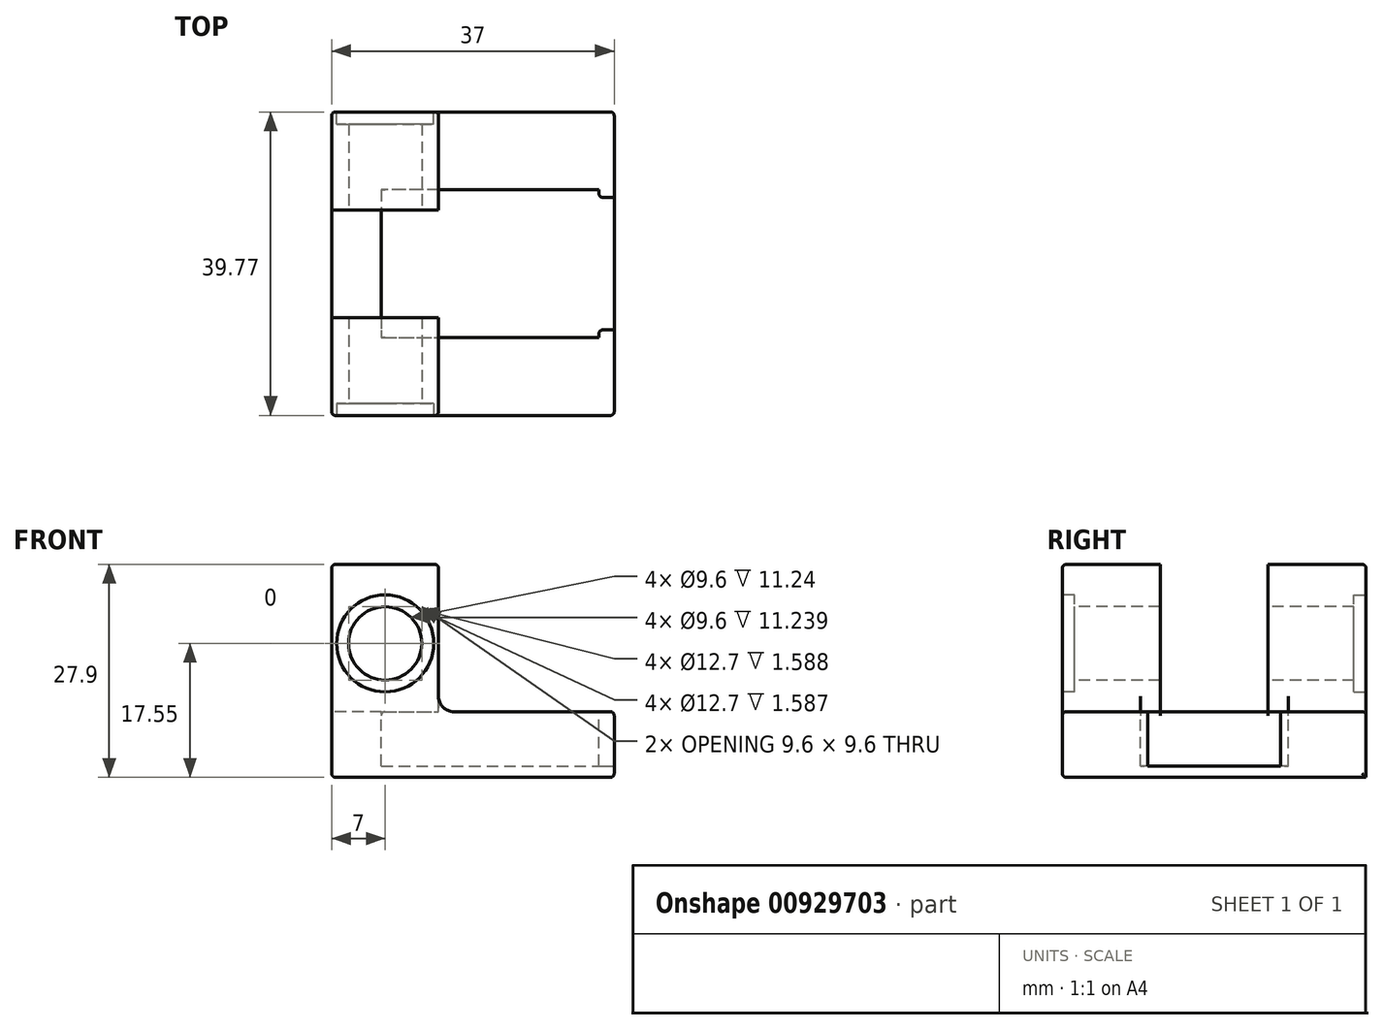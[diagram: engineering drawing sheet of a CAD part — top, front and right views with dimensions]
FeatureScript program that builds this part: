
annotation { "Feature Type Name" : "Feature", "Feature Type Description" : "" }
export const myFeature = defineFeature(function(context is Context, id is Id, definition is map)
    precondition{}
    {
        {
            var Q0;
            Q0=qCreatedBy(makeId("Front.planeOp"),FACE);
            var sketch = newSketch(context, id + "F0", { "sketchPlane" : qUnion([Q0])});
            skLineSegment(sketch, "E0", {"start": v(0, 0) * mm, "end": v(0, 27.9) * mm});
            skLineSegment(sketch, "E1", {"start": v(0, 27.9) * mm, "end": v(14, 27.9) * mm});
            skLineSegment(sketch, "E2", {"start": v(14, 27.9) * mm, "end": v(14, 8.6) * mm});
            skLineSegment(sketch, "E3", {"start": v(14, 8.6) * mm, "end": v(37, 8.6) * mm});
            skLineSegment(sketch, "E4", {"start": v(37, 8.6) * mm, "end": v(37, 0) * mm});
            skLineSegment(sketch, "E5", {"start": v(37, 0) * mm, "end": v(0, 0) * mm});
            skSolve(sketch);
        }
        {
            var Q0;
            Q0=makeQuery(id+"F0.imprint","IMPRINT",FACE,{"disambiguationData":[TD([[makeQuery(id+"F0.imprint","IMPRINT",EDGE,{"derivedFrom":sQuery(id+"F0.wireOp",EDGE,"E0")}),-1.0]])]});
            extrude(context, id + "F1", {"entities" : qUnion([Q0]), "depth" : 39.77 * mm, "offsetDistance" : 25 * mm});
        }
        {
            var Q0;
            Q0=makeQuery(id+"F1.opExtrude","CAP_FACE",FACE,{"disambiguationData":[OSD([sQuery(id+"F0.wireOp",EDGE,"E0"),sQuery(id+"F0.wireOp",EDGE,"E1"),sQuery(id+"F0.wireOp",EDGE,"E2"),sQuery(id+"F0.wireOp",EDGE,"E3"),sQuery(id+"F0.wireOp",EDGE,"E4"),sQuery(id+"F0.wireOp",EDGE,"E5")])],"isStart":false});
            var sketch = newSketch(context, id + "F2", { "sketchPlane" : qUnion([Q0])});
            skLineSegment(sketch, "E6", {"start": v(7, 27.9) * mm, "end": v(7, 23.9) * mm, "construction": true});
            skLineSegment(sketch, "E7", {"start": v(7, 23.9) * mm, "end": v(7, 0) * mm, "construction": true});
            skLineSegment(sketch, "E8", {"start": v(7, 23.9) * mm, "end": v(7, 17.55) * mm, "construction": true});
            skCircle(sketch, "E9", {"center": v(7, 17.55) * mm, "radius": 6.35 * mm});
            skCircle(sketch, "E10", {"center": v(7, 17.55) * mm, "radius": 4.8 * mm});
            skSolve(sketch);
        }
        {
            var Q0;
            Q0=makeQuery(id+"F2.imprint","IMPRINT",FACE,{"disambiguationData":[TD([[makeQuery(id+"F2.imprint","IMPRINT",EDGE,{"derivedFrom":sQuery(id+"F2.wireOp",EDGE,"E10")}),1.0]])]});
            extrude(context, id + "F3", {"entities" : qUnion([Q0]), "operationType" : NewBodyOperationType.REMOVE, "endBound" : BoundingType.THROUGH_ALL, "oppositeDirection" : true, "depth" : 25 * mm, "offsetDistance" : 25 * mm});
        }
        {
            var Q0;
            Q0=makeQuery(id+"F2.imprint","IMPRINT",FACE,{"disambiguationData":[TD([[makeQuery(id+"F2.imprint","IMPRINT",EDGE,{"derivedFrom":sQuery(id+"F2.wireOp",EDGE,"E9")}),1.0]])]});
            extrude(context, id + "F4", {"entities" : qUnion([Q0]), "operationType" : NewBodyOperationType.REMOVE, "oppositeDirection" : true, "depth" : 1.59 * mm, "offsetDistance" : 25 * mm});
        }
        {
            var Q0;
            Q0=makeQuery(id+"F0.imprint","IMPRINT",FACE,{"disambiguationData":[TD([[makeQuery(id+"F0.imprint","IMPRINT",EDGE,{"derivedFrom":sQuery(id+"F0.wireOp",EDGE,"E0")}),-1.0]])]});
            var sketch = newSketch(context, id + "F5", { "sketchPlane" : qUnion([Q0])});
            skCircle(sketch, "E11", {"center": v(7, 17.55) * mm, "radius": 6.35 * mm});
            skSolve(sketch);
        }
        {
            var Q0;
            Q0=makeQuery(id+"F5.imprint","IMPRINT",FACE,{"disambiguationData":[TD([[makeQuery(id+"F5.imprint","IMPRINT",EDGE,{"derivedFrom":sQuery(id+"F5.wireOp",EDGE,"E11")}),1.0]])]});
            extrude(context, id + "F6", {"entities" : qUnion([Q0]), "operationType" : NewBodyOperationType.REMOVE, "depth" : 1.59 * mm, "offsetDistance" : 25 * mm});
        }
        {
            var Q0;
            Q0=makeQuery(id+"F1.opExtrude","SWEPT_FACE",FACE,{"disambiguationData":[OSD([sQuery(id+"F0.wireOp",EDGE,"E3")])]});
            var sketch = newSketch(context, id + "F7", { "sketchPlane" : qUnion([Q0])});
            skLineSegment(sketch, "E12", {"start": v(37, -11.2) * mm, "end": v(35, -11.2) * mm});
            skLineSegment(sketch, "E13", {"start": v(35, -11.2) * mm, "end": v(35, -10.2) * mm});
            skLineSegment(sketch, "E14", {"start": v(35, -10.2) * mm, "end": v(6.5, -10.2) * mm});
            skLineSegment(sketch, "E15", {"start": v(6.5, -10.2) * mm, "end": v(6.5, -29.56) * mm});
            skLineSegment(sketch, "E16", {"start": v(6.5, -29.56) * mm, "end": v(35, -29.56) * mm});
            skLineSegment(sketch, "E17", {"start": v(35, -29.56) * mm, "end": v(35, -28.56) * mm});
            skLineSegment(sketch, "E18", {"start": v(35, -28.56) * mm, "end": v(37, -28.56) * mm});
            skLineSegment(sketch, "E19", {"start": v(37, -11.2) * mm, "end": v(37, -28.56) * mm});
            skSolve(sketch);
        }
        {
            var Q0;
            {var subQ0=sQuery(id+"F7.wireOp",EDGE,"E15");Q0=makeQuery(id+"F7.imprint","IMPRINT",FACE,{"disambiguationData":[TD([[makeQuery(id+"F7.imprint","IMPRINT",EDGE,{"derivedFrom":subQ0}),1.0]])]});}
            var Q1;
            Q1=makeQuery(id+"F7.imprint","IMPRINT",FACE,{"disambiguationData":[TD([[makeQuery(id+"F7.imprint","IMPRINT",EDGE,{"derivedFrom":sQuery(id+"F7.wireOp",EDGE,"E12")}),1.0]])]});
            extrude(context, id + "F8", {"entities" : qUnion([Q0, Q1]), "operationType" : NewBodyOperationType.REMOVE, "oppositeDirection" : true, "depth" : 7.1 * mm, "offsetDistance" : 25 * mm});
        }
        {
            var Q0;
            Q0=makeQuery(id+"F1.opExtrude","SWEPT_FACE",FACE,{"disambiguationData":[OSD([sQuery(id+"F0.wireOp",EDGE,"E1")])]});
            var sketch = newSketch(context, id + "F9", { "sketchPlane" : qUnion([Q0])});
            skLineSegment(sketch, "E20", {"start": v(0, -19.88) * mm, "end": v(0, -12.83) * mm});
            skLineSegment(sketch, "E21", {"start": v(0, -12.83) * mm, "end": v(14, -12.83) * mm});
            skLineSegment(sketch, "E22", {"start": v(14, -12.83) * mm, "end": v(14, -26.94) * mm});
            skLineSegment(sketch, "E23", {"start": v(14, -26.94) * mm, "end": v(0, -26.94) * mm});
            skLineSegment(sketch, "E24", {"start": v(0, -26.94) * mm, "end": v(0, -19.88) * mm});
            skSolve(sketch);
        }
        {
            var Q0;
            Q0=makeQuery(id+"F9.imprint","IMPRINT",FACE,{"disambiguationData":[TD([[makeQuery(id+"F9.imprint","IMPRINT",EDGE,{"derivedFrom":sQuery(id+"F9.wireOp",EDGE,"E20")}),-1.0]])]});
            var Q1;
            Q1=makeQuery(id+"F8.boolean.opBoolean","COPY",FACE,{"derivedFrom":makeQuery(id+"F8.opExtrude","CAP_FACE",FACE,{"disambiguationData":[OSD([sQuery(id+"F7.wireOp",EDGE,"E12"),sQuery(id+"F7.wireOp",EDGE,"E13"),sQuery(id+"F7.wireOp",EDGE,"E14"),sQuery(id+"F7.wireOp",EDGE,"E15"),sQuery(id+"F7.wireOp",EDGE,"E16"),sQuery(id+"F7.wireOp",EDGE,"E17"),sQuery(id+"F7.wireOp",EDGE,"E18"),sQuery(id+"F7.wireOp",EDGE,"E19")])],"isStart":true})});
            extrude(context, id + "F10", {"entities" : qUnion([Q0]), "operationType" : NewBodyOperationType.REMOVE, "endBound" : BoundingType.UP_TO_SURFACE, "oppositeDirection" : true, "depth" : 25 * mm, "endBoundEntityFace" : qUnion([Q1]), "offsetDistance" : 25 * mm});
        }
        {
            var Q0;
            {var subQ0=sQuery(id+"F9.wireOp",EDGE,"E23");Q0=makeQuery(id+"F10.boolean.opBoolean","COPY",EDGE,{"disambiguationData":[topologyDisambiguationEdgeConnected([makeQuery(id+"F8.boolean.opBoolean","COPY",FACE,{"derivedFrom":makeQuery(id+"F8.opExtrude","CAP_FACE",FACE,{"disambiguationData":[OSD([sQuery(id+"F7.wireOp",EDGE,"E12"),sQuery(id+"F7.wireOp",EDGE,"E13"),sQuery(id+"F7.wireOp",EDGE,"E14"),sQuery(id+"F7.wireOp",EDGE,"E15"),sQuery(id+"F7.wireOp",EDGE,"E16"),sQuery(id+"F7.wireOp",EDGE,"E17"),sQuery(id+"F7.wireOp",EDGE,"E18"),sQuery(id+"F7.wireOp",EDGE,"E19")])],"isStart":true})})])],"derivedFrom":makeQuery(id+"F10.opExtrude","CAP_EDGE",EDGE,{"disambiguationData":[OSD([subQ0])],"isStart":false})});}
            var Q1;
            {var subQ0=sQuery(id+"F7.wireOp",EDGE,"E16");var subQ1=makeQuery(id+"F8.opExtrude","CAP_FACE",FACE,{"disambiguationData":[OSD([sQuery(id+"F7.wireOp",EDGE,"E12"),sQuery(id+"F7.wireOp",EDGE,"E13"),sQuery(id+"F7.wireOp",EDGE,"E14"),sQuery(id+"F7.wireOp",EDGE,"E15"),subQ0,sQuery(id+"F7.wireOp",EDGE,"E17"),sQuery(id+"F7.wireOp",EDGE,"E18"),sQuery(id+"F7.wireOp",EDGE,"E19")])],"isStart":true});var subQ2=sQuery(id+"F0.wireOp",EDGE,"E3");var subQ3=sQuery(id+"F0.wireOp",EDGE,"E2");var subQ4=makeQuery(id+"F1.opExtrude","SWEPT_FACE",FACE,{"disambiguationData":[OSD([subQ3])]});Q1=makeQuery(id+"F10.boolean.opBoolean","SPLIT",EDGE,{"disambiguationData":[TD([makeQuery(id+"F8.boolean.opBoolean","COPY",FACE,{"derivedFrom":makeQuery(id+"F8.opExtrude","SWEPT_FACE",FACE,{"disambiguationData":[OSD([subQ0])]})})])],"derivedFrom":makeQuery(id+"F8.boolean.opBoolean","SPLIT",EDGE,{"disambiguationData":[topologyDisambiguationEdgeConnected([subQ4,subQ1])],"derivedFrom":makeQuery(id+"F1.opExtrude","SWEPT_EDGE",EDGE,{"disambiguationData":[OSD([subQ3,subQ2])]})})});}
            var Q2;
            {var subQ0=sQuery(id+"F9.wireOp",EDGE,"E21");Q2=makeQuery(id+"F10.boolean.opBoolean","COPY",EDGE,{"disambiguationData":[topologyDisambiguationEdgeConnected([makeQuery(id+"F8.boolean.opBoolean","COPY",FACE,{"derivedFrom":makeQuery(id+"F8.opExtrude","CAP_FACE",FACE,{"disambiguationData":[OSD([sQuery(id+"F7.wireOp",EDGE,"E12"),sQuery(id+"F7.wireOp",EDGE,"E13"),sQuery(id+"F7.wireOp",EDGE,"E14"),sQuery(id+"F7.wireOp",EDGE,"E15"),sQuery(id+"F7.wireOp",EDGE,"E16"),sQuery(id+"F7.wireOp",EDGE,"E17"),sQuery(id+"F7.wireOp",EDGE,"E18"),sQuery(id+"F7.wireOp",EDGE,"E19")])],"isStart":true})})])],"derivedFrom":makeQuery(id+"F10.opExtrude","CAP_EDGE",EDGE,{"disambiguationData":[OSD([subQ0])],"isStart":false})});}
            var Q3;
            {var subQ0=sQuery(id+"F7.wireOp",EDGE,"E14");var subQ1=sQuery(id+"F0.wireOp",EDGE,"E3");var subQ2=makeQuery(id+"F8.opExtrude","CAP_FACE",FACE,{"disambiguationData":[OSD([sQuery(id+"F7.wireOp",EDGE,"E12"),sQuery(id+"F7.wireOp",EDGE,"E13"),subQ0,sQuery(id+"F7.wireOp",EDGE,"E15"),sQuery(id+"F7.wireOp",EDGE,"E16"),sQuery(id+"F7.wireOp",EDGE,"E17"),sQuery(id+"F7.wireOp",EDGE,"E18"),sQuery(id+"F7.wireOp",EDGE,"E19")])],"isStart":true});var subQ3=sQuery(id+"F0.wireOp",EDGE,"E2");var subQ4=makeQuery(id+"F1.opExtrude","SWEPT_FACE",FACE,{"disambiguationData":[OSD([subQ3])]});Q3=makeQuery(id+"F10.boolean.opBoolean","SPLIT",EDGE,{"disambiguationData":[TD([makeQuery(id+"F8.boolean.opBoolean","COPY",FACE,{"derivedFrom":makeQuery(id+"F8.opExtrude","SWEPT_FACE",FACE,{"disambiguationData":[OSD([subQ0])]})})])],"derivedFrom":makeQuery(id+"F8.boolean.opBoolean","SPLIT",EDGE,{"disambiguationData":[topologyDisambiguationEdgeConnected([subQ4,subQ2])],"derivedFrom":makeQuery(id+"F1.opExtrude","SWEPT_EDGE",EDGE,{"disambiguationData":[OSD([subQ3,subQ1])]})})});}
            fillet(context, id + "F11", {"entities" : qUnion([Q0, Q1, Q2, Q3]), "radius" : 2 * mm, "tangentPropagation" : true, "allowEdgeOverflow" : false});
        }
        {
            var Q0;
            {var subQ0=sQuery(id+"F7.wireOp",EDGE,"E14");Q0=makeQuery(id+"F8.boolean.opBoolean","COPY",EDGE,{"disambiguationData":[topologyDisambiguationEdgeConnected([makeQuery(id+"F1.opExtrude","SWEPT_FACE",FACE,{"disambiguationData":[OSD([sQuery(id+"F0.wireOp",EDGE,"E3")])]})])],"derivedFrom":makeQuery(id+"F8.opExtrude","CAP_EDGE",EDGE,{"disambiguationData":[OSD([subQ0])],"isStart":true})});}
            var Q1;
            {var subQ0=sQuery(id+"F7.wireOp",EDGE,"E16");Q1=makeQuery(id+"F8.boolean.opBoolean","COPY",EDGE,{"disambiguationData":[topologyDisambiguationEdgeConnected([makeQuery(id+"F1.opExtrude","SWEPT_FACE",FACE,{"disambiguationData":[OSD([sQuery(id+"F0.wireOp",EDGE,"E3")])]})])],"derivedFrom":makeQuery(id+"F8.opExtrude","CAP_EDGE",EDGE,{"disambiguationData":[OSD([subQ0])],"isStart":true})});}
            var Q2;
            {var subQ0=sQuery(id+"F7.wireOp",EDGE,"E15");Q2=makeQuery(id+"F10.boolean.opBoolean","SPLIT",EDGE,{"disambiguationData":[topologyDisambiguationEdgeConnected([makeQuery(id+"F8.boolean.opBoolean","COPY",FACE,{"derivedFrom":makeQuery(id+"F8.opExtrude","SWEPT_FACE",FACE,{"disambiguationData":[OSD([subQ0])]})}),makeQuery(id+"F10.opExtrude","CAP_FACE",FACE,{"disambiguationData":[OSD([sQuery(id+"F9.wireOp",EDGE,"E20"),sQuery(id+"F9.wireOp",EDGE,"E21"),sQuery(id+"F9.wireOp",EDGE,"E22"),sQuery(id+"F9.wireOp",EDGE,"E23"),sQuery(id+"F9.wireOp",EDGE,"E24")])],"isStart":false})])],"derivedFrom":makeQuery(id+"F8.boolean.opBoolean","COPY",EDGE,{"derivedFrom":makeQuery(id+"F8.opExtrude","CAP_EDGE",EDGE,{"disambiguationData":[OSD([subQ0])],"isStart":true})})});}
            var Q3;
            {var subQ0=sQuery(id+"F0.wireOp",EDGE,"E4");var subQ1=sQuery(id+"F0.wireOp",EDGE,"E3");Q3=makeQuery(id+"F8.boolean.opBoolean","SPLIT",EDGE,{"disambiguationData":[TD([makeQuery(id+"F8.opExtrude","SWEPT_FACE",FACE,{"disambiguationData":[OSD([sQuery(id+"F7.wireOp",EDGE,"E12")])]})])],"derivedFrom":makeQuery(id+"F1.opExtrude","SWEPT_EDGE",EDGE,{"disambiguationData":[OSD([subQ1,subQ0])]})});}
            var Q4;
            {var subQ0=sQuery(id+"F0.wireOp",EDGE,"E4");var subQ1=sQuery(id+"F0.wireOp",EDGE,"E3");Q4=makeQuery(id+"F8.boolean.opBoolean","SPLIT",EDGE,{"disambiguationData":[TD([makeQuery(id+"F8.opExtrude","SWEPT_FACE",FACE,{"disambiguationData":[OSD([sQuery(id+"F7.wireOp",EDGE,"E18")])]})])],"derivedFrom":makeQuery(id+"F1.opExtrude","SWEPT_EDGE",EDGE,{"disambiguationData":[OSD([subQ1,subQ0])]})});}
            var Q5;
            Q5=makeQuery(id+"F8.boolean.opBoolean","COPY",EDGE,{"derivedFrom":makeQuery(id+"F8.opExtrude","SWEPT_EDGE",EDGE,{"disambiguationData":[OSD([sQuery(id+"F0.wireOp",EDGE,"E3"),sQuery(id+"F0.wireOp",EDGE,"E4"),sQuery(id+"F7.wireOp",EDGE,"E18"),sQuery(id+"F7.wireOp",EDGE,"E19")])]})});
            var Q6;
            Q6=makeQuery(id+"F8.boolean.opBoolean","COPY",EDGE,{"derivedFrom":makeQuery(id+"F8.opExtrude","SWEPT_EDGE",EDGE,{"disambiguationData":[OSD([sQuery(id+"F7.wireOp",EDGE,"E12"),sQuery(id+"F7.wireOp",EDGE,"E13")])]})});
            var Q7;
            Q7=makeQuery(id+"F8.boolean.opBoolean","COPY",EDGE,{"derivedFrom":makeQuery(id+"F8.opExtrude","CAP_EDGE",EDGE,{"disambiguationData":[OSD([sQuery(id+"F7.wireOp",EDGE,"E19")])],"isStart":false})});
            var Q8;
            Q8=makeQuery(id+"F8.boolean.opBoolean","COPY",EDGE,{"derivedFrom":makeQuery(id+"F8.opExtrude","CAP_EDGE",EDGE,{"disambiguationData":[OSD([sQuery(id+"F7.wireOp",EDGE,"E17")])],"isStart":true})});
            var Q9;
            Q9=makeQuery(id+"F8.boolean.opBoolean","COPY",EDGE,{"derivedFrom":makeQuery(id+"F8.opExtrude","SWEPT_EDGE",EDGE,{"disambiguationData":[OSD([sQuery(id+"F7.wireOp",EDGE,"E17"),sQuery(id+"F7.wireOp",EDGE,"E18")])]})});
            var Q10;
            Q10=makeQuery(id+"F8.boolean.opBoolean","COPY",EDGE,{"derivedFrom":makeQuery(id+"F8.opExtrude","CAP_EDGE",EDGE,{"disambiguationData":[OSD([sQuery(id+"F7.wireOp",EDGE,"E18")])],"isStart":true})});
            var Q11;
            Q11=makeQuery(id+"F8.boolean.opBoolean","COPY",EDGE,{"derivedFrom":makeQuery(id+"F8.opExtrude","CAP_EDGE",EDGE,{"disambiguationData":[OSD([sQuery(id+"F7.wireOp",EDGE,"E12")])],"isStart":true})});
            var Q12;
            Q12=makeQuery(id+"F8.boolean.opBoolean","COPY",EDGE,{"derivedFrom":makeQuery(id+"F8.opExtrude","CAP_EDGE",EDGE,{"disambiguationData":[OSD([sQuery(id+"F7.wireOp",EDGE,"E13")])],"isStart":true})});
            var Q13;
            Q13=makeQuery(id+"F1.opExtrude","CAP_EDGE",EDGE,{"disambiguationData":[OSD([sQuery(id+"F0.wireOp",EDGE,"E3")])],"isStart":true});
            var Q14;
            Q14=makeQuery(id+"F1.opExtrude","CAP_EDGE",EDGE,{"disambiguationData":[OSD([sQuery(id+"F0.wireOp",EDGE,"E3")])],"isStart":false});
            var Q15;
            {var subQ0=sQuery(id+"F0.wireOp",EDGE,"E2");var subQ1=sQuery(id+"F0.wireOp",EDGE,"E1");Q15=makeQuery(id+"F10.boolean.opBoolean","SPLIT",EDGE,{"disambiguationData":[TD([makeQuery(id+"F10.opExtrude","SWEPT_FACE",FACE,{"disambiguationData":[OSD([sQuery(id+"F9.wireOp",EDGE,"E23")])]})])],"derivedFrom":makeQuery(id+"F1.opExtrude","SWEPT_EDGE",EDGE,{"disambiguationData":[OSD([subQ1,subQ0])]})});}
            var Q16;
            Q16=makeQuery(id+"F10.boolean.opBoolean","COPY",EDGE,{"derivedFrom":makeQuery(id+"F10.opExtrude","CAP_EDGE",EDGE,{"disambiguationData":[OSD([sQuery(id+"F9.wireOp",EDGE,"E23")])],"isStart":true})});
            var Q17;
            {var subQ0=sQuery(id+"F0.wireOp",EDGE,"E0");var subQ1=sQuery(id+"F0.wireOp",EDGE,"E1");Q17=makeQuery(id+"F10.boolean.opBoolean","SPLIT",EDGE,{"disambiguationData":[TD([makeQuery(id+"F10.opExtrude","SWEPT_FACE",FACE,{"disambiguationData":[OSD([sQuery(id+"F9.wireOp",EDGE,"E23")])]})])],"derivedFrom":makeQuery(id+"F1.opExtrude","SWEPT_EDGE",EDGE,{"disambiguationData":[OSD([subQ0,subQ1])]})});}
            var Q18;
            Q18=makeQuery(id+"F1.opExtrude","CAP_EDGE",EDGE,{"disambiguationData":[OSD([sQuery(id+"F0.wireOp",EDGE,"E1")])],"isStart":false});
            var Q19;
            Q19=makeQuery(id+"F10.boolean.opBoolean","COPY",EDGE,{"derivedFrom":makeQuery(id+"F10.opExtrude","CAP_EDGE",EDGE,{"disambiguationData":[OSD([sQuery(id+"F9.wireOp",EDGE,"E21")])],"isStart":true})});
            var Q20;
            Q20=makeQuery(id+"F10.boolean.opBoolean","COPY",EDGE,{"derivedFrom":makeQuery(id+"F10.opExtrude","CAP_EDGE",EDGE,{"disambiguationData":[OSD([sQuery(id+"F9.wireOp",EDGE,"E20"),sQuery(id+"F9.wireOp",EDGE,"E24")])],"isStart":false})});
            var Q21;
            {var subQ0=sQuery(id+"F0.wireOp",EDGE,"E0");var subQ1=sQuery(id+"F0.wireOp",EDGE,"E1");Q21=makeQuery(id+"F10.boolean.opBoolean","SPLIT",EDGE,{"disambiguationData":[TD([makeQuery(id+"F10.opExtrude","SWEPT_FACE",FACE,{"disambiguationData":[OSD([sQuery(id+"F9.wireOp",EDGE,"E21")])]})])],"derivedFrom":makeQuery(id+"F1.opExtrude","SWEPT_EDGE",EDGE,{"disambiguationData":[OSD([subQ0,subQ1])]})});}
            var Q22;
            Q22=makeQuery(id+"F1.opExtrude","CAP_EDGE",EDGE,{"disambiguationData":[OSD([sQuery(id+"F0.wireOp",EDGE,"E1")])],"isStart":true});
            var Q23;
            {var subQ0=sQuery(id+"F0.wireOp",EDGE,"E2");var subQ1=sQuery(id+"F0.wireOp",EDGE,"E1");Q23=makeQuery(id+"F10.boolean.opBoolean","SPLIT",EDGE,{"disambiguationData":[TD([makeQuery(id+"F10.opExtrude","SWEPT_FACE",FACE,{"disambiguationData":[OSD([sQuery(id+"F9.wireOp",EDGE,"E21")])]})])],"derivedFrom":makeQuery(id+"F1.opExtrude","SWEPT_EDGE",EDGE,{"disambiguationData":[OSD([subQ1,subQ0])]})});}
            var Q24;
            Q24=makeQuery(id+"F10.boolean.opBoolean","COPY",EDGE,{"derivedFrom":makeQuery(id+"F10.opExtrude","SWEPT_EDGE",EDGE,{"disambiguationData":[OSD([sQuery(id+"F0.wireOp",EDGE,"E1"),sQuery(id+"F0.wireOp",EDGE,"E2"),sQuery(id+"F9.wireOp",EDGE,"E21"),sQuery(id+"F9.wireOp",EDGE,"E22")])]})});
            var Q25;
            Q25=makeQuery(id+"F10.boolean.opBoolean","COPY",EDGE,{"derivedFrom":makeQuery(id+"F10.opExtrude","SWEPT_EDGE",EDGE,{"disambiguationData":[OSD([sQuery(id+"F0.wireOp",EDGE,"E0"),sQuery(id+"F0.wireOp",EDGE,"E1"),sQuery(id+"F9.wireOp",EDGE,"E20"),sQuery(id+"F9.wireOp",EDGE,"E21")])]})});
            var Q26;
            Q26=makeQuery(id+"F1.opExtrude","CAP_EDGE",EDGE,{"disambiguationData":[OSD([sQuery(id+"F0.wireOp",EDGE,"E0")])],"isStart":true});
            var Q27;
            Q27=makeQuery(id+"F1.opExtrude","SWEPT_EDGE",EDGE,{"disambiguationData":[OSD([sQuery(id+"F0.wireOp",EDGE,"E0"),sQuery(id+"F0.wireOp",EDGE,"E5")])]});
            var Q28;
            Q28=makeQuery(id+"F1.opExtrude","CAP_EDGE",EDGE,{"disambiguationData":[OSD([sQuery(id+"F0.wireOp",EDGE,"E0")])],"isStart":false});
            var Q29;
            Q29=makeQuery(id+"F1.opExtrude","CAP_EDGE",EDGE,{"disambiguationData":[OSD([sQuery(id+"F0.wireOp",EDGE,"E2")])],"isStart":false});
            var Q30;
            Q30=makeQuery(id+"F10.boolean.opBoolean","COPY",EDGE,{"derivedFrom":makeQuery(id+"F10.opExtrude","SWEPT_EDGE",EDGE,{"disambiguationData":[OSD([sQuery(id+"F0.wireOp",EDGE,"E1"),sQuery(id+"F0.wireOp",EDGE,"E2"),sQuery(id+"F9.wireOp",EDGE,"E22"),sQuery(id+"F9.wireOp",EDGE,"E23")])]})});
            var Q31;
            Q31=makeQuery(id+"F1.opExtrude","CAP_EDGE",EDGE,{"disambiguationData":[OSD([sQuery(id+"F0.wireOp",EDGE,"E2")])],"isStart":true});
            var Q32;
            Q32=makeQuery(id+"F1.opExtrude","CAP_EDGE",EDGE,{"disambiguationData":[OSD([sQuery(id+"F0.wireOp",EDGE,"E5")])],"isStart":false});
            var Q33;
            Q33=makeQuery(id+"F1.opExtrude","SWEPT_EDGE",EDGE,{"disambiguationData":[OSD([sQuery(id+"F0.wireOp",EDGE,"E4"),sQuery(id+"F0.wireOp",EDGE,"E5")])]});
            var Q34;
            Q34=makeQuery(id+"F1.opExtrude","CAP_EDGE",EDGE,{"disambiguationData":[OSD([sQuery(id+"F0.wireOp",EDGE,"E4")])],"isStart":false});
            var Q35;
            Q35=makeQuery(id+"F1.opExtrude","CAP_EDGE",EDGE,{"disambiguationData":[OSD([sQuery(id+"F0.wireOp",EDGE,"E4")])],"isStart":true});
            var Q36;
            Q36=makeQuery(id+"F10.boolean.opBoolean","COPY",EDGE,{"derivedFrom":makeQuery(id+"F10.opExtrude","SWEPT_EDGE",EDGE,{"disambiguationData":[OSD([sQuery(id+"F0.wireOp",EDGE,"E0"),sQuery(id+"F0.wireOp",EDGE,"E1"),sQuery(id+"F9.wireOp",EDGE,"E23"),sQuery(id+"F9.wireOp",EDGE,"E24")])]})});
            fillet(context, id + "F12", {"entities" : qUnion([Q0, Q1, Q2, Q3, Q4, Q5, Q6, Q7, Q8, Q9, Q10, Q11, Q12, Q13, Q14, Q15, Q16, Q17, Q18, Q19, Q20, Q21, Q22, Q23, Q24, Q25, Q26, Q27, Q28, Q29, Q30, Q31, Q32, Q33, Q34, Q35, Q36]), "radius" : 0.5 * mm, "tangentPropagation" : true, "allowEdgeOverflow" : false});
        }
    });
